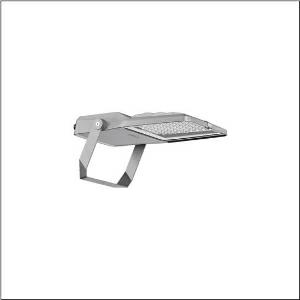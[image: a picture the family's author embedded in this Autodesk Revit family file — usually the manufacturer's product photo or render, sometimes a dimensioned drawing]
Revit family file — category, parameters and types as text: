
# Revit family: floodlight_fl_21_iq_mini___rs12_5xa7772b4b1a_ec65
name_source: partatom
category: Lighting Fixtures
units: mm (PartAtom-declared; Revit-internal decimal feet)

## family parameters
Cut with Voids When Loaded = No
Host = Face
Light Source = No
Part Type = Normal
Room Calculation Point = No
Round Connector Dimension = Use Diameter
Shared = No

## types (1)
- --- (1 x LED, 6560 lm, 45.5 W, 4000K)
    Apparent Load = 46 VA
    CIE Flux Codes = 79 92 99 100 100
    Color Rendering = 70
    Color Temperature = 4000K
    Default Elevation = 1800 mm
    Description = Floodlight FL 21 iQ mini, floodlight, primary light control with lens, of PMMA, primary optical cover: protective disc, of toughened safety glass, transparent, light distribution: RS12, light emission: direct distribution, installation type: surface-mounted, LED, High Power LED, rated luminous flux: 6.560lm, luminous efficacy: 144lm/W, light colour: 740, colour temperature: 4000K, control gear: iQ Street-Remote/DALI, control: Street-Remote, Auto-Match, Temp-Guard, Night-Set, Smart-Wire, Desk-Remote (wireless, voltage-free reading and setting of iQ features in the workshop via application-optimized NFC function/RFID function), optimised constant luminous flux control (CLO 2.0), with terminal, 6-pole, mains connection: 220..240V, AC, 50/60Hz, start of lifetime: 46W, end of service life: 48W, reduction: 22W, luminaire housing, of diecast aluminium, powder-coated, Siteco® metallic grey (DB 702S), corrosivity category C5 mid according to DIN EN ISO 12944, suitable for swimming pools, chlorine-resistant, sealing non-destructively replaceable, mounting bracket, of steel, galvanised, powder-coated, Siteco® metallic grey (DB 702S), protection rating (complete): IP66, insulation class (complete): insulation class II (safety insulation), certification: CE, ENEC, VDE, protection symbol: D, impact resistance: IK08, permissible operating ambient temperature: -40..+40°C, permissible operating ambient temperature for outdoor applications: -40..+50°C, standard: DIN EN 12944, LABS conformity tested according to VDMA 24364:2018-05, packaging unit: 1 piece

Light Distribution: RS12
    Height = 70 mm
    Lamp = 1 x LED
    Lamp Light Flux = 6560 lm
    Lamp Power = 45.5 W
    Lamp count = 1
    Length = 485 mm
    Luminous efficacy = 144 lm/W
    Manufacturer = Siteco
    ModVariant = No
    Model = 5XA7772B4B1A
    Number of Poles = 1
    OnlyDefault = Yes
    Power Factor = 1
    Product Name = Floodlight FL 21 iQ mini | RS12
    Product group = floodlight | pylon annexe
    ProductGroupID = 6200
    Protection Class = Protection class II
    Protection Degree = IP 66
    RLX_Detail_Level = 1
    RLX_Emergency_Light_Flux = 0 lm
    RLX_Emergency_Type = 0
    RLX_Emergency_Type_DB = No
    RlxData = <blob elided: 90937 chars, md5=918b8c58>
    Socket = socket
    Standby Power = 0 W
    System Light Flux = 6560 lm
    System Power = 46 W
    Type Comments = factory setting: luminous flux: 100 % | dim-lin: 254 | 463 mA
    Type Image = l_1006845.jpg
    URL = http://relux.com
    VarID = @adj_167816
    Voltage = 0 V
    Weight = 0.00 kg
    Width = 337 mm

## geometry (parser evidence)
native form markers: Blend x4, Sweep x13
no freeform markers — native parametric forms only
